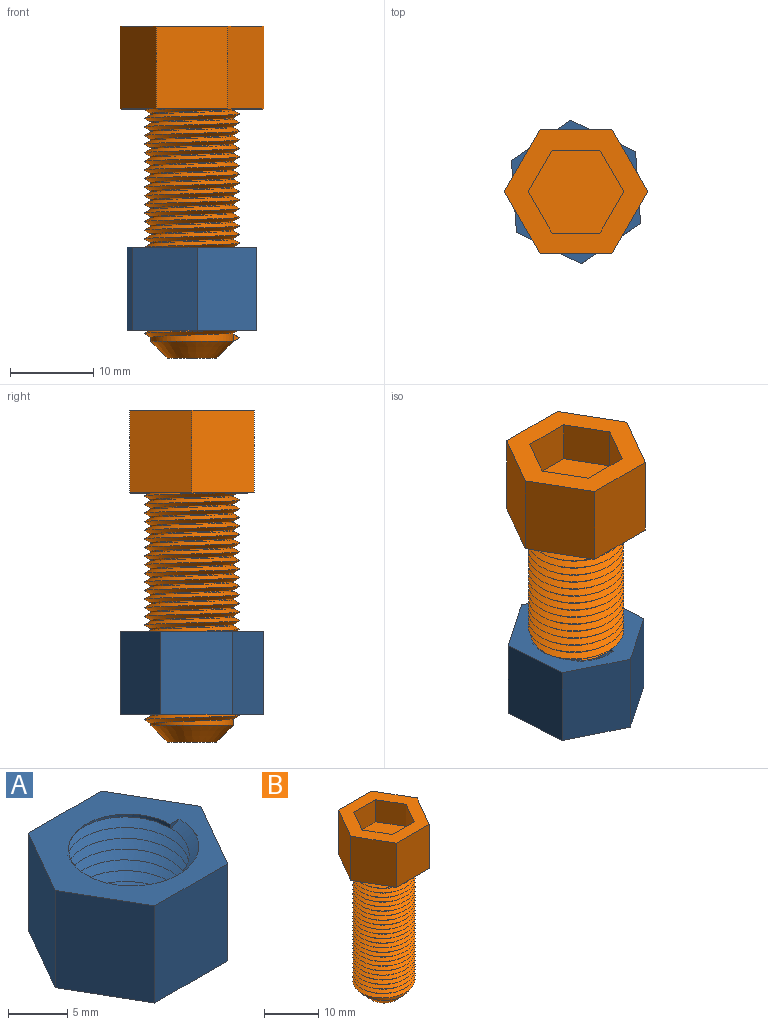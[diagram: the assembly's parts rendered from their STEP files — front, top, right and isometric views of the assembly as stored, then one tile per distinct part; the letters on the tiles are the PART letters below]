
ASSEMBLY  parts=2 mates=1
PART A: 16 faces, bbox 18.2x15.9x12 mm
  f0: cylinder r=5mm len=8.87mm, axis (0,0,-1), area 2.7mm2, adj f1,f10,f13
  f1: plane 18.18x15.85mm, normal (0,0,1), area 104.3mm2, adj f0,f2,f3,f4,f5,f6,f8,f10
  f2: plane 10x8.66mm, normal (0,-1,0), area 86.6mm2, adj f1,f3,f8,f9
  f3: plane 10x7.5mm, normal (0.87,-0.5,0), area 86.6mm2, adj f1,f2,f4,f9
  f4: plane 10x7.5mm, normal (0.87,0.5,0), area 86.6mm2, adj f1,f3,f5,f9
  f5: plane 10x8.66mm, normal (0,1,0), area 86.6mm2, adj f1,f4,f6,f9
  f6: plane 10x7.5mm, normal (-0.87,0.5,0), area 86.6mm2, adj f1,f5,f8,f9
  f7: cylinder r=5mm len=9.83mm, axis (0,0,-1), area 3.7mm2, adj f9,f11,f14
  f8: plane 10x7.5mm, normal (-0.87,-0.5,0), area 86.6mm2, adj f1,f2,f6,f9
  f9: plane 17.35x15.03mm, normal (0,0,-1), area 106.9mm2, adj f2,f3,f4,f5,f6,f7,f8,f11
  f10: bspline ~10.29x5.94mm, area 2.3mm2, adj f0,f1,f13,f15
  f11: bspline ~10.4x10.29mm, area 2.6mm2, adj f7,f9,f12,f14
  f12: bspline ~14.1x12.21mm, area 346.5mm2, adj f1,f9,f11,f13,f14,f15
  f13: plane 1.04x0.52mm, normal (0,-1,0), area 0.3mm2, adj f0,f1,f10,f12
  f14: plane 1.11x0.59mm, normal (0,1,0), area 0.4mm2, adj f7,f9,f11,f12,f15
  f15: bspline ~14.1x12.21mm, area 343.6mm2, adj f1,f10,f12,f14
PART B: 21 faces, bbox 17.9x15.6x40.6 mm
  f0: plane 10x8.66mm, normal (0,1,0), area 86.6mm2, adj f1,f5,f6,f7
  f1: plane 10x7.5mm, normal (-0.87,0.5,0), area 86.6mm2, adj f0,f2,f6,f7
  f2: plane 10x7.5mm, normal (-0.87,-0.5,0), area 86.6mm2, adj f1,f3,f6,f7
  f3: plane 10x8.66mm, normal (0,-1,0), area 86.6mm2, adj f2,f4,f6,f7
  f4: plane 10x7.5mm, normal (0.87,-0.5,0), area 86.6mm2, adj f3,f5,f6,f7
  f5: plane 10x7.5mm, normal (0.87,0.5,0), area 86.6mm2, adj f0,f4,f6,f7
  f6: plane 17.32x15mm, normal (0,0,1), area 108.3mm2, adj f0,f1,f2,f3,f4,f5,f8,f9
  f7: plane 17.88x15.56mm, normal (0,0,-1), area 106mm2, adj f0,f1,f2,f3,f4,f5,f15,f18
  f8: plane 5x5mm, normal (-0.87,0.5,0), area 28.9mm2, adj f6,f9,f13,f14
  f9: plane 5x5mm, normal (-0.87,-0.5,0), area 28.9mm2, adj f6,f8,f10,f14
  f10: plane 5.77x5mm, normal (0,-1,0), area 28.9mm2, adj f6,f9,f11,f14
  f11: plane 5x5mm, normal (0.87,-0.5,0), area 28.9mm2, adj f6,f10,f12,f14
  f12: plane 5x5mm, normal (0.87,0.5,0), area 28.9mm2, adj f6,f11,f13,f14
  f13: plane 5.77x5mm, normal (0,1,0), area 28.9mm2, adj f6,f8,f12,f14
  f14: plane 11.55x10mm, normal (0,0,1), area 86.6mm2, adj f8,f9,f10,f11,f12,f13
  f15: cylinder r=5mm len=28mm, axis (0,0,1), area 346.2mm2, adj f7,f17,f18,f19,f20
  f16: plane 6x6mm, normal (0,0,-1), area 28.3mm2, adj f17
  f17: cone r=3mm half-angle=45deg, axis (0,0,1), area 71.1mm2, adj f15,f16
  f18: bspline ~28.43x13.28mm, area 783.5mm2, adj f7,f15,f19,f20
  f19: bspline ~28.09x13.28mm, area 772.6mm2, adj f7,f15,f18,f20
  f20: plane 0.87x0.75mm, normal (0,-1,0), area 0.3mm2, adj f15,f18,f19
PLACE A rot(axis=(0,0,-1),85.9deg) t=(-16.98,-0.57,-51.55)mm
PLACE B t=(-16.98,-0.57,-24.91)mm fixed
MATE cylindrical B.f15 <-> A.f0  axis (0,0,1) through (-16.98,-0.57,-38.91)mm
